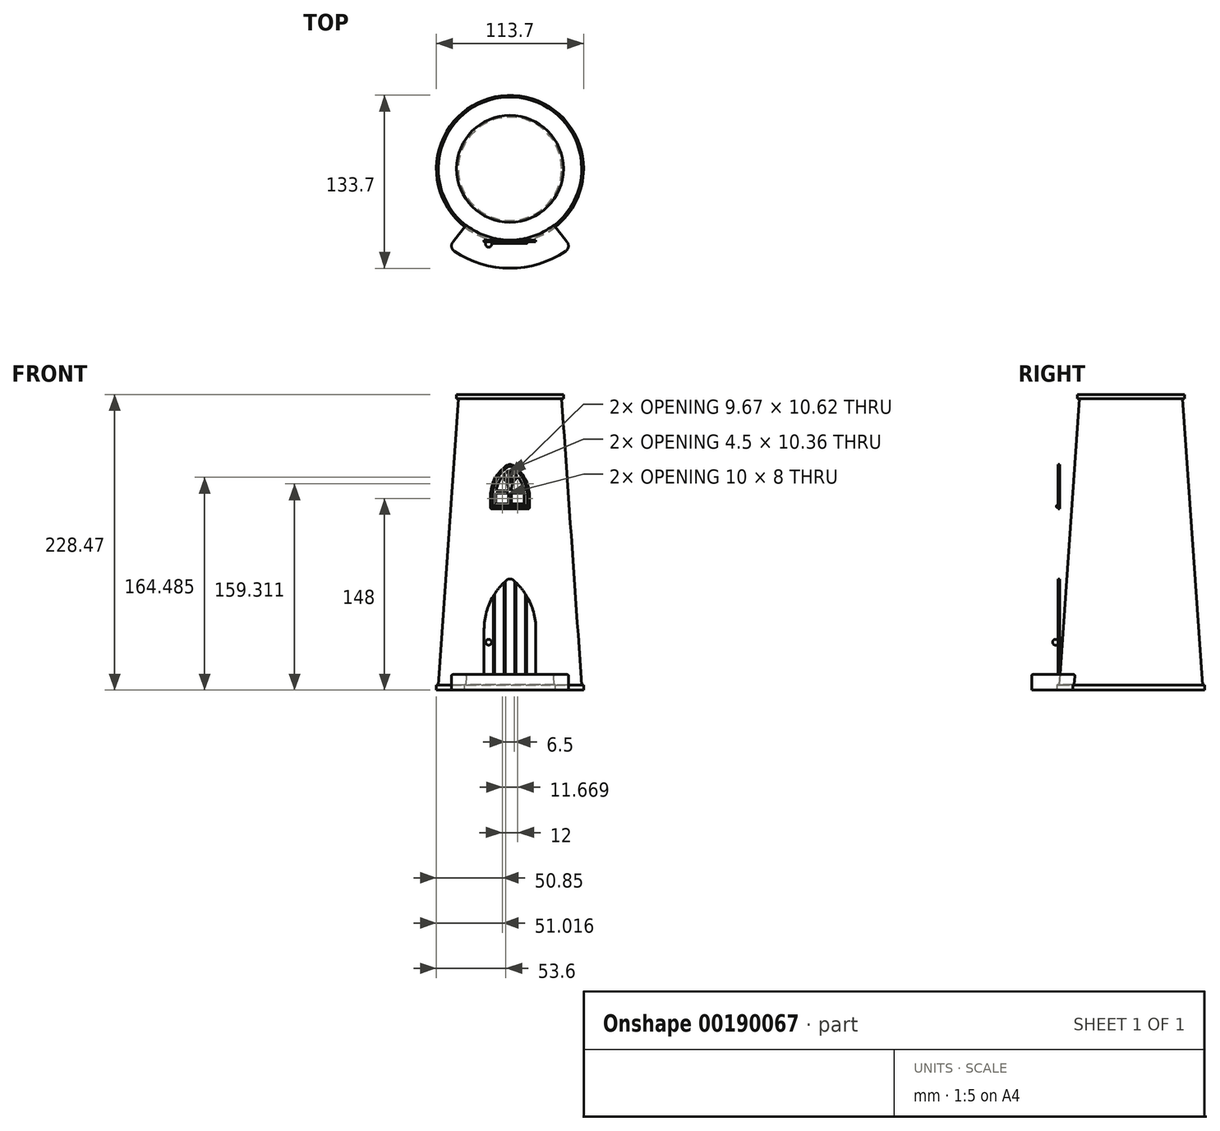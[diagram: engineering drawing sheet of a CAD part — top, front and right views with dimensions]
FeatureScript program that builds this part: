
annotation { "Feature Type Name" : "Feature", "Feature Type Description" : "" }
export const myFeature = defineFeature(function(context is Context, id is Id, definition is map)
    precondition{}
    {
        {
            var Q0;
            Q0=qCreatedBy(makeId("Front.planeOp"),FACE);
            var sketch = newSketch(context, id + "F0", { "sketchPlane" : qUnion([Q0])});
            skLineSegment(sketch, "E0", {"start": v(0, 0) * mm, "end": v(56.85, 0) * mm});
            skLineSegment(sketch, "E1", {"start": v(56.85, 0) * mm, "end": v(56.85, 4) * mm});
            skLineSegment(sketch, "E2", {"start": v(56.85, 4) * mm, "end": v(55.45, 4) * mm});
            skLineSegment(sketch, "E3", {"start": v(55.45, 4) * mm, "end": v(39.9, 225.27) * mm});
            skLineSegment(sketch, "E4", {"start": v(39.9, 225.27) * mm, "end": v(41.3, 225.27) * mm});
            skLineSegment(sketch, "E5", {"start": v(41.3, 225.27) * mm, "end": v(41.3, 228.47) * mm});
            skLineSegment(sketch, "E6", {"start": v(41.3, 228.47) * mm, "end": v(0, 228.47) * mm});
            skLineSegment(sketch, "E7", {"start": v(0, 228.47) * mm, "end": v(0, 0) * mm});
            skSolve(sketch);
        }
        {
            var Q0;
            Q0=makeQuery(id+"F0.imprint","IMPRINT",FACE,{"disambiguationData":[TD([[makeQuery(id+"F0.imprint","IMPRINT",EDGE,{"derivedFrom":sQuery(id+"F0.wireOp",EDGE,"E0")}),1.0]])]});
            var Q1;
            Q1=sQuery(id+"F0.wireOp",EDGE,"E7");
            revolve(context, id + "F1", {"entities" : qUnion([Q0]), "axis" : qUnion([Q1]), "revolveType" : RevolveType.FULL});
        }
        {
            var Q0;
            Q0=qCreatedBy(makeId("Top.planeOp"),FACE);
            cPlane(context, id + "F2", {"entities" : qUnion([Q0]), "cplaneType" : CPlaneType.OFFSET, "offset" : 12 * mm, "width" : 150 * mm, "height" : 150 * mm});
        }
        {
            var Q0;
            Q0=qCreatedBy(id+"F2.planeOp",FACE);
            var sketch = newSketch(context, id + "F3", { "sketchPlane" : qUnion([Q0])});
            skCircle(sketch, "E8", {"center": v(0, 0) * mm, "radius": 54.89 * mm});
            skArc(sketch, "E9.0", {"start": v(-35, -44.8) * mm, "mid": v(0, -56.85) * mm, "end": v(35, -44.8) * mm, "construction": true});
            skArc(sketch, "E10.0", {"start": v(-47.31, -60.56) * mm, "mid": v(0, -76.85) * mm, "end": v(47.31, -60.56) * mm});
            skLineSegment(sketch, "E11", {"start": v(-47.31, -60.56) * mm, "end": v(-33.8, -43.25) * mm});
            skLineSegment(sketch, "E12", {"start": v(-33.8, -43.25) * mm, "end": v(33.8, -43.25) * mm});
            skLineSegment(sketch, "E13", {"start": v(33.8, -43.25) * mm, "end": v(47.31, -60.56) * mm});
            skSolve(sketch);
        }
        {
            var Q0;
            Q0=makeQuery(id+"F3.imprint","IMPRINT",FACE,{"disambiguationData":[TD([[makeQuery(id+"F3.imprint","IMPRINT",EDGE,{"derivedFrom":sQuery(id+"F3.wireOp",EDGE,"E10.0")}),1.0]])]});
            var Q1;
            Q1=makeQuery(id+"F1.opRevolve","SWEPT_FACE",FACE,{"disambiguationData":[OSD([sQuery(id+"F0.wireOp",EDGE,"E0")])]});
            extrude(context, id + "F4", {"entities" : qUnion([Q0]), "endBound" : BoundingType.UP_TO_SURFACE, "oppositeDirection" : true, "endBoundEntityFace" : qUnion([Q1]), "depth" : 25 * mm});
        }
        {
            var Q0;
            Q0=makeQuery(id+"F1.opRevolve","SWEPT_BODY",BODY,{"disambiguationData":[OSD([sQuery(id+"F0.wireOp",EDGE,"E0"),sQuery(id+"F0.wireOp",EDGE,"E1"),sQuery(id+"F0.wireOp",EDGE,"E2"),sQuery(id+"F0.wireOp",EDGE,"E3"),sQuery(id+"F0.wireOp",EDGE,"E4"),sQuery(id+"F0.wireOp",EDGE,"E5"),sQuery(id+"F0.wireOp",EDGE,"E6"),sQuery(id+"F0.wireOp",EDGE,"E7")])]});
            var Q1;
            Q1=makeQuery(id+"F4.opExtrude","SWEPT_BODY",BODY,{"disambiguationData":[OSD([sQuery(id+"F3.wireOp",EDGE,"E8"),sQuery(id+"F3.wireOp",EDGE,"E10.0"),sQuery(id+"F3.wireOp",EDGE,"E11"),sQuery(id+"F3.wireOp",EDGE,"E13")])]});
            var Q2;
            Q2=makeQuery(id+"F1.opRevolve","SWEPT_FACE",FACE,{"disambiguationData":[OSD([sQuery(id+"F0.wireOp",EDGE,"E3")])]});
            var Q3;
            Q3=makeQuery(id+"F1.opRevolve","SWEPT_FACE",FACE,{"disambiguationData":[OSD([sQuery(id+"F0.wireOp",EDGE,"E1")])]});
            var Q4;
            Q4=makeQuery(id+"F1.opRevolve","SWEPT_FACE",FACE,{"disambiguationData":[OSD([sQuery(id+"F0.wireOp",EDGE,"E2")])]});
            booleanBodies(context, id + "F5", {"operationType" : BooleanOperationType.SUBTRACTION, "tools" : qUnion([Q0]), "targets" : qUnion([Q1]), "offset" : true, "entitiesToOffset" : qUnion([Q2, Q3, Q4]), "offsetDistance" : .2 * mm, "keepTools" : true});
        }
        {
            var Q0;
            Q0=makeQuery(id+"F4.opExtrude","SWEPT_EDGE",EDGE,{"disambiguationData":[OSD([sQuery(id+"F3.wireOp",EDGE,"E10.0"),sQuery(id+"F3.wireOp",EDGE,"E13")])]});
            var Q1;
            Q1=makeQuery(id+"F4.opExtrude","SWEPT_EDGE",EDGE,{"disambiguationData":[OSD([sQuery(id+"F3.wireOp",EDGE,"E10.0"),sQuery(id+"F3.wireOp",EDGE,"E11")])]});
            fillet(context, id + "F6", {"entities" : qUnion([Q0, Q1]), "radius" : 5 * mm, "tangentPropagation" : true, "allowEdgeOverflow" : false});
        }
        {
            var Q0;
            Q0=makeQuery(id+"F4.opExtrude","CAP_EDGE",EDGE,{"disambiguationData":[OSD([sQuery(id+"F3.wireOp",EDGE,"E10.0")])],"isStart":true});
            fillet(context, id + "F7", {"entities" : qUnion([Q0]), "radius" : 1 * mm, "tangentPropagation" : true, "allowEdgeOverflow" : false});
        }
        {
            var Q0;
            Q0=qCreatedBy(makeId("Front.planeOp"),FACE);
            cPlane(context, id + "F8", {"entities" : qUnion([Q0]), "cplaneType" : CPlaneType.OFFSET, "offset" : 55 * mm, "width" : 150 * mm, "height" : 150 * mm});
        }
        {
            var Q0;
            Q0=qCreatedBy(id+"F8.planeOp",FACE);
            var sketch = newSketch(context, id + "F9", { "sketchPlane" : qUnion([Q0])});
            skLineSegment(sketch, "E14.0", {"start": v(33.12, 12) * mm, "end": v(-33.12, 12) * mm, "construction": true});
            skLineSegment(sketch, "E15.bottom", {"start": v(20, 12) * mm, "end": v(-20, 12) * mm});
            skLineSegment(sketch, "E15.left", {"start": v(20, 12) * mm, "end": v(20, 47) * mm});
            skLineSegment(sketch, "E15.right", {"start": v(-20, 12) * mm, "end": v(-20, 47) * mm});
            skPoint(sketch, "E15.middle", {"position": v(0, 41.56) * mm});
            skLineSegment(sketch, "E16", {"start": v(-3.5, 84.12) * mm, "end": v(-3.5, 12) * mm});
            skLineSegment(sketch, "E17", {"start": v(3.5, 84.12) * mm, "end": v(3.5, 12) * mm});
            skLineSegment(sketch, "E18", {"start": v(4.75, 82.95) * mm, "end": v(4.75, 12) * mm});
            skLineSegment(sketch, "E19", {"start": v(11.75, 74.51) * mm, "end": v(11.75, 12) * mm});
            skLineSegment(sketch, "E20", {"start": v(13, 72.51) * mm, "end": v(13, 12) * mm});
            skLineSegment(sketch, "E21.MirrorCS", {"start": v(-4.75, 82.95) * mm, "end": v(-4.75, 12) * mm});
            skLineSegment(sketch, "E22.MirrorCS", {"start": v(-11.75, 74.51) * mm, "end": v(-11.75, 12) * mm});
            skLineSegment(sketch, "E23.MirrorCS", {"start": v(-13, 72.51) * mm, "end": v(-13, 12) * mm});
            skLineSegment(sketch, "E24", {"start": v(0, 18.3) * mm, "end": v(0, 101.07) * mm, "construction": true});
            skArc(sketch, "E25", {"start": v(-2.6, 84.9) * mm, "mid": v(-15.44, 67.85) * mm, "end": v(-20, 47) * mm});
            skArc(sketch, "E26.MirrorCS", {"start": v(2.6, 84.9) * mm, "mid": v(15.44, 67.85) * mm, "end": v(20, 47) * mm});
            skPoint(sketch, "E27.visualSharp", {"position": v(0, 87) * mm});
            skArc(sketch, "E27.filletArc", {"start": v(2.6, 84.9) * mm, "mid": v(0, 85.87) * mm, "end": v(-2.6, 84.9) * mm});
            skSolve(sketch);
        }
        {
            var Q0;
            {var subQ0=sQuery(id+"F9.wireOp",EDGE,"E15.right");Q0=makeQuery(id+"F9.imprint","IMPRINT",FACE,{"disambiguationData":[TD([[makeQuery(id+"F9.imprint","IMPRINT",EDGE,{"derivedFrom":subQ0}),-1.0]])]});}
            var Q1;
            {var subQ0=sQuery(id+"F9.wireOp",EDGE,"E21.MirrorCS");Q1=makeQuery(id+"F9.imprint","IMPRINT",FACE,{"disambiguationData":[TD([[makeQuery(id+"F9.imprint","IMPRINT",EDGE,{"derivedFrom":subQ0}),-1.0]])]});}
            var Q2;
            {var subQ0=sQuery(id+"F9.wireOp",EDGE,"E16");Q2=makeQuery(id+"F9.imprint","IMPRINT",FACE,{"disambiguationData":[TD([[makeQuery(id+"F9.imprint","IMPRINT",EDGE,{"derivedFrom":subQ0}),1.0]])]});}
            var Q3;
            {var subQ0=sQuery(id+"F9.wireOp",EDGE,"E18");Q3=makeQuery(id+"F9.imprint","IMPRINT",FACE,{"disambiguationData":[TD([[makeQuery(id+"F9.imprint","IMPRINT",EDGE,{"derivedFrom":subQ0}),1.0]])]});}
            var Q4;
            {var subQ0=sQuery(id+"F9.wireOp",EDGE,"E15.left");Q4=makeQuery(id+"F9.imprint","IMPRINT",FACE,{"disambiguationData":[TD([[makeQuery(id+"F9.imprint","IMPRINT",EDGE,{"derivedFrom":subQ0}),1.0]])]});}
            extrude(context, id + "F10", {"entities" : qUnion([Q0, Q1, Q2, Q3, Q4]), "depth" : 1.5 * mm});
        }
        {
            var Q0;
            {var subQ0=sQuery(id+"F9.wireOp",EDGE,"E22.MirrorCS");Q0=makeQuery(id+"F9.imprint","IMPRINT",FACE,{"disambiguationData":[TD([[makeQuery(id+"F9.imprint","IMPRINT",EDGE,{"derivedFrom":subQ0}),-1.0]])]});}
            var Q1;
            {var subQ0=sQuery(id+"F9.wireOp",EDGE,"E16");Q1=makeQuery(id+"F9.imprint","IMPRINT",FACE,{"disambiguationData":[TD([[makeQuery(id+"F9.imprint","IMPRINT",EDGE,{"derivedFrom":subQ0}),-1.0]])]});}
            var Q2;
            {var subQ0=sQuery(id+"F9.wireOp",EDGE,"E17");Q2=makeQuery(id+"F9.imprint","IMPRINT",FACE,{"disambiguationData":[TD([[makeQuery(id+"F9.imprint","IMPRINT",EDGE,{"derivedFrom":subQ0}),1.0]])]});}
            var Q3;
            {var subQ0=sQuery(id+"F9.wireOp",EDGE,"E19");Q3=makeQuery(id+"F9.imprint","IMPRINT",FACE,{"disambiguationData":[TD([[makeQuery(id+"F9.imprint","IMPRINT",EDGE,{"derivedFrom":subQ0}),1.0]])]});}
            extrude(context, id + "F11", {"entities" : qUnion([Q0, Q1, Q2, Q3]), "operationType" : NewBodyOperationType.ADD, "depth" : .75 * mm});
        }
        {
            var Q0;
            Q0=makeQuery(id+"F10.opExtrude","CAP_FACE",FACE,{"disambiguationData":[OSD([sQuery(id+"F9.wireOp",EDGE,"E15.bottom"),sQuery(id+"F9.wireOp",EDGE,"E15.right"),sQuery(id+"F9.wireOp",EDGE,"GGup5s7j-cwvR-bdwB-zDN7-7esyc12EIQJO"),sQuery(id+"F9.wireOp",EDGE,"E23.MirrorCS")])],"isStart":false});
            var sketch = newSketch(context, id + "F12", { "sketchPlane" : qUnion([Q0])});
            skCircle(sketch, "E28", {"center": v(-16.5, 37) * mm, "radius": 2.25 * mm});
            skLineSegment(sketch, "E29", {"start": v(-20, 37) * mm, "end": v(-13, 37) * mm, "construction": true});
            skSolve(sketch);
        }
        {
            var Q0;
            Q0=makeQuery(id+"F12.imprint","IMPRINT",FACE,{"disambiguationData":[TD([[makeQuery(id+"F12.imprint","IMPRINT",EDGE,{"derivedFrom":sQuery(id+"F12.wireOp",EDGE,"E28")}),1.0]])]});
            extrude(context, id + "F13", {"entities" : qUnion([Q0]), "operationType" : NewBodyOperationType.ADD, "depth" : 4 * mm});
        }
        {
            var Q0;
            Q0=makeQuery(id+"F13.opExtrude","CAP_EDGE",EDGE,{"disambiguationData":[OSD([sQuery(id+"F12.wireOp",EDGE,"E28")])],"isStart":false});
            fillet(context, id + "F14", {"entities" : qUnion([Q0]), "radius" : 2 * mm, "tangentPropagation" : true, "allowEdgeOverflow" : false});
        }
        {
            var Q0;
            Q0=qCreatedBy(id+"F8.planeOp",FACE);
            var sketch = newSketch(context, id + "F15", { "sketchPlane" : qUnion([Q0])});
            skLineSegment(sketch, "E30.bottom", {"start": v(15, 140) * mm, "end": v(-15, 140) * mm});
            skLineSegment(sketch, "E30.left", {"start": v(15, 140) * mm, "end": v(15, 150) * mm});
            skLineSegment(sketch, "E30.right", {"start": v(-15, 140) * mm, "end": v(-15, 150) * mm});
            skLineSegment(sketch, "E31", {"start": v(0, 122.8) * mm, "end": v(0, 228.47) * mm, "construction": true});
            skArc(sketch, "E32", {"start": v(-2.2, 173.7) * mm, "mid": v(-11.6, 163.47) * mm, "end": v(-15, 150) * mm});
            skArc(sketch, "E33.MirrorCS", {"start": v(2.2, 173.7) * mm, "mid": v(11.6, 163.47) * mm, "end": v(15, 150) * mm});
            skPoint(sketch, "E34.visualSharp", {"position": v(0, 175) * mm});
            skArc(sketch, "E34.filletArc", {"start": v(2.2, 173.7) * mm, "mid": v(0, 174.36) * mm, "end": v(-2.2, 173.7) * mm});
            skLineSegment(sketch, "E35.0", {"start": v(-41.3, 228.47) * mm, "end": v(41.3, 228.47) * mm, "construction": true});
            skLineSegment(sketch, "E36.0", {"start": v(-11, 144) * mm, "end": v(-11, 150) * mm});
            skArc(sketch, "E36.1", {"start": v(-1, 169.66) * mm, "mid": v(-7.37, 162.78) * mm, "end": v(-10.67, 154) * mm});
            skLineSegment(sketch, "E36.2", {"start": v(11, 144) * mm, "end": v(1, 144) * mm});
            skLineSegment(sketch, "E36.3", {"start": v(11, 144) * mm, "end": v(11, 150) * mm});
            skArc(sketch, "E36.4", {"start": v(1, 169.66) * mm, "mid": v(7.37, 162.78) * mm, "end": v(10.67, 154) * mm});
            skLineSegment(sketch, "E37", {"start": v(1, 169.66) * mm, "end": v(1, 159.3) * mm});
            skLineSegment(sketch, "E38", {"start": v(-1, 169.66) * mm, "end": v(-1, 159.3) * mm});
            skLineSegment(sketch, "E39", {"start": v(-10.67, 154) * mm, "end": v(-1, 154) * mm});
            skLineSegment(sketch, "E40", {"start": v(-10.92, 152) * mm, "end": v(-1, 152) * mm});
            skArc(sketch, "E41.trimOffspring", {"start": v(10.92, 152) * mm, "mid": v(10.98, 151) * mm, "end": v(11, 150) * mm});
            skArc(sketch, "E42.trimOffspring", {"start": v(-10.92, 152) * mm, "mid": v(-10.98, 151) * mm, "end": v(-11, 150) * mm});
            skLineSegment(sketch, "E43.trimOffspring", {"start": v(1, 154) * mm, "end": v(10.67, 154) * mm});
            skLineSegment(sketch, "E44.trimOffspring", {"start": v(1, 152) * mm, "end": v(10.92, 152) * mm});
            skLineSegment(sketch, "E45.trimOffspring", {"start": v(-1, 152) * mm, "end": v(-1, 144) * mm});
            skLineSegment(sketch, "E46.trimOffspring", {"start": v(1, 152) * mm, "end": v(1, 144) * mm});
            skLineSegment(sketch, "E47.trimOffspring", {"start": v(-1, 144) * mm, "end": v(-11, 144) * mm});
            skArc(sketch, "E48", {"start": v(-1, 154) * mm, "mid": v(-2.35, 159.9) * mm, "end": v(-6.12, 164.62) * mm});
            skArc(sketch, "E49.0", {"start": v(0, 154) * mm, "mid": v(-1.45, 160.33) * mm, "end": v(-5.5, 165.4) * mm});
            skArc(sketch, "E50.MirrorCS", {"start": v(0, 154) * mm, "mid": v(1.45, 160.33) * mm, "end": v(5.5, 165.4) * mm});
            skArc(sketch, "E51.MirrorCS", {"start": v(1, 154) * mm, "mid": v(2.35, 159.9) * mm, "end": v(6.12, 164.62) * mm});
            skSolve(sketch);
        }
        {
            var Q0;
            Q0 = qSketchRegion(id + "F15", true);
            extrude(context, id + "F16", {"entities" : qUnion([Q0]), "depth" : .75 * mm});
        }
        {
            var Q0;
            Q0=makeQuery(id+"F16.opExtrude","CAP_FACE",FACE,{"disambiguationData":[OSD([sQuery(id+"F15.wireOp",EDGE,"E30.bottom"),sQuery(id+"F15.wireOp",EDGE,"E30.left"),sQuery(id+"F15.wireOp",EDGE,"E30.right"),sQuery(id+"F15.wireOp",EDGE,"E32"),sQuery(id+"F15.wireOp",EDGE,"E33.MirrorCS"),sQuery(id+"F15.wireOp",EDGE,"E34.filletArc"),sQuery(id+"F15.wireOp",EDGE,"E36.0"),sQuery(id+"F15.wireOp",EDGE,"E36.1"),sQuery(id+"F15.wireOp",EDGE,"E36.2"),sQuery(id+"F15.wireOp",EDGE,"E36.3"),sQuery(id+"F15.wireOp",EDGE,"E36.4"),sQuery(id+"F15.wireOp",EDGE,"E37"),sQuery(id+"F15.wireOp",EDGE,"E38"),sQuery(id+"F15.wireOp",EDGE,"E39"),sQuery(id+"F15.wireOp",EDGE,"E40"),sQuery(id+"F15.wireOp",EDGE,"E41.trimOffspring"),sQuery(id+"F15.wireOp",EDGE,"E42.trimOffspring"),sQuery(id+"F15.wireOp",EDGE,"E43.trimOffspring"),sQuery(id+"F15.wireOp",EDGE,"E44.trimOffspring"),sQuery(id+"F15.wireOp",EDGE,"E45.trimOffspring"),sQuery(id+"F15.wireOp",EDGE,"E46.trimOffspring"),sQuery(id+"F15.wireOp",EDGE,"E47.trimOffspring"),sQuery(id+"F15.wireOp",EDGE,"E48"),sQuery(id+"F15.wireOp",EDGE,"E49.0"),sQuery(id+"F15.wireOp",EDGE,"E50.MirrorCS"),sQuery(id+"F15.wireOp",EDGE,"E51.MirrorCS")])],"isStart":false});
            var sketch = newSketch(context, id + "F17", { "sketchPlane" : qUnion([Q0])});
            skLineSegment(sketch, "E52.0", {"start": v(13.5, 141.5) * mm, "end": v(13.5, 150) * mm});
            skArc(sketch, "E52.1", {"start": v(1.07, 172.64) * mm, "mid": v(10.19, 162.91) * mm, "end": v(13.5, 150) * mm});
            skArc(sketch, "E52.2", {"start": v(-1.07, 172.64) * mm, "mid": v(-10.19, 162.91) * mm, "end": v(-13.5, 150) * mm});
            skLineSegment(sketch, "E52.3", {"start": v(-13.5, 141.5) * mm, "end": v(-13.5, 150) * mm});
            skPoint(sketch, "E53.visualSharp", {"position": v(0, 173.29) * mm});
            skArc(sketch, "E53.filletArc", {"start": v(1.07, 172.64) * mm, "mid": v(0, 172.95) * mm, "end": v(-1.07, 172.64) * mm});
            skLineSegment(sketch, "E54.0", {"start": v(12.5, 142.5) * mm, "end": v(12.5, 150) * mm});
            skLineSegment(sketch, "E54.1", {"start": v(-12.5, 142.5) * mm, "end": v(12.5, 142.5) * mm});
            skArc(sketch, "E54.2", {"start": v(12.5, 150) * mm, "mid": v(9.31, 162.43) * mm, "end": v(0.54, 171.8) * mm});
            skArc(sketch, "E54.3", {"start": v(-0.54, 171.8) * mm, "mid": v(-9.31, 162.43) * mm, "end": v(-12.5, 150) * mm});
            skLineSegment(sketch, "E54.4", {"start": v(-12.5, 150) * mm, "end": v(-12.5, 142.5) * mm});
            skPoint(sketch, "E55.visualSharp", {"position": v(0, 172.13) * mm});
            skArc(sketch, "E55.filletArc", {"start": v(0.54, 171.8) * mm, "mid": v(0, 171.95) * mm, "end": v(-0.54, 171.8) * mm});
            skLineSegment(sketch, "E56", {"start": v(13.5, 141.5) * mm, "end": v(-13.5, 141.5) * mm});
            skLineSegment(sketch, "E57", {"start": v(12.5, 142.5) * mm, "end": v(13.5, 142.5) * mm});
            skLineSegment(sketch, "E58", {"start": v(-12.5, 142.5) * mm, "end": v(-13.5, 142.5) * mm});
            skSolve(sketch);
        }
        {
            var Q0;
            {var subQ3=sQuery(id+"F17.wireOp",EDGE,"E52.1");Q0=makeQuery(id+"F17.imprint","IMPRINT",FACE,{"disambiguationData":[TD([[makeQuery(id+"F17.imprint","IMPRINT",EDGE,{"derivedFrom":subQ3}),-1.0]])]});}
            extrude(context, id + "F18", {"entities" : qUnion([Q0]), "operationType" : NewBodyOperationType.ADD, "depth" : .75 * mm});
        }
        {
            var Q0;
            Q0=makeQuery(id+"F17.imprint","IMPRINT",FACE,{"disambiguationData":[TD([[makeQuery(id+"F17.imprint","IMPRINT",EDGE,{"derivedFrom":sQuery(id+"F17.wireOp",EDGE,"E54.1")}),-1.0]])]});
            extrude(context, id + "F19", {"entities" : qUnion([Q0]), "operationType" : NewBodyOperationType.ADD, "depth" : 2 * mm});
        }
        {
            var Q0;
            Q0=makeQuery(id+"F19.opExtrude","CAP_EDGE",EDGE,{"disambiguationData":[OSD([sQuery(id+"F17.wireOp",EDGE,"E52.3")])],"isStart":false});
            var Q1;
            Q1=makeQuery(id+"F19.opExtrude","CAP_EDGE",EDGE,{"disambiguationData":[OSD([sQuery(id+"F17.wireOp",EDGE,"E52.0")])],"isStart":false});
            var Q2;
            Q2=makeQuery(id+"F16.opExtrude","SWEPT_EDGE",EDGE,{"disambiguationData":[OSD([sQuery(id+"F15.wireOp",EDGE,"E30.bottom"),sQuery(id+"F15.wireOp",EDGE,"E30.right")])]});
            var Q3;
            Q3=makeQuery(id+"F16.opExtrude","SWEPT_EDGE",EDGE,{"disambiguationData":[OSD([sQuery(id+"F15.wireOp",EDGE,"E30.bottom"),sQuery(id+"F15.wireOp",EDGE,"E30.left")])]});
            fillet(context, id + "F20", {"entities" : qUnion([Q0, Q1, Q2, Q3]), "radius" : 1 * mm, "tangentPropagation" : true, "allowEdgeOverflow" : false});
        }
    });
